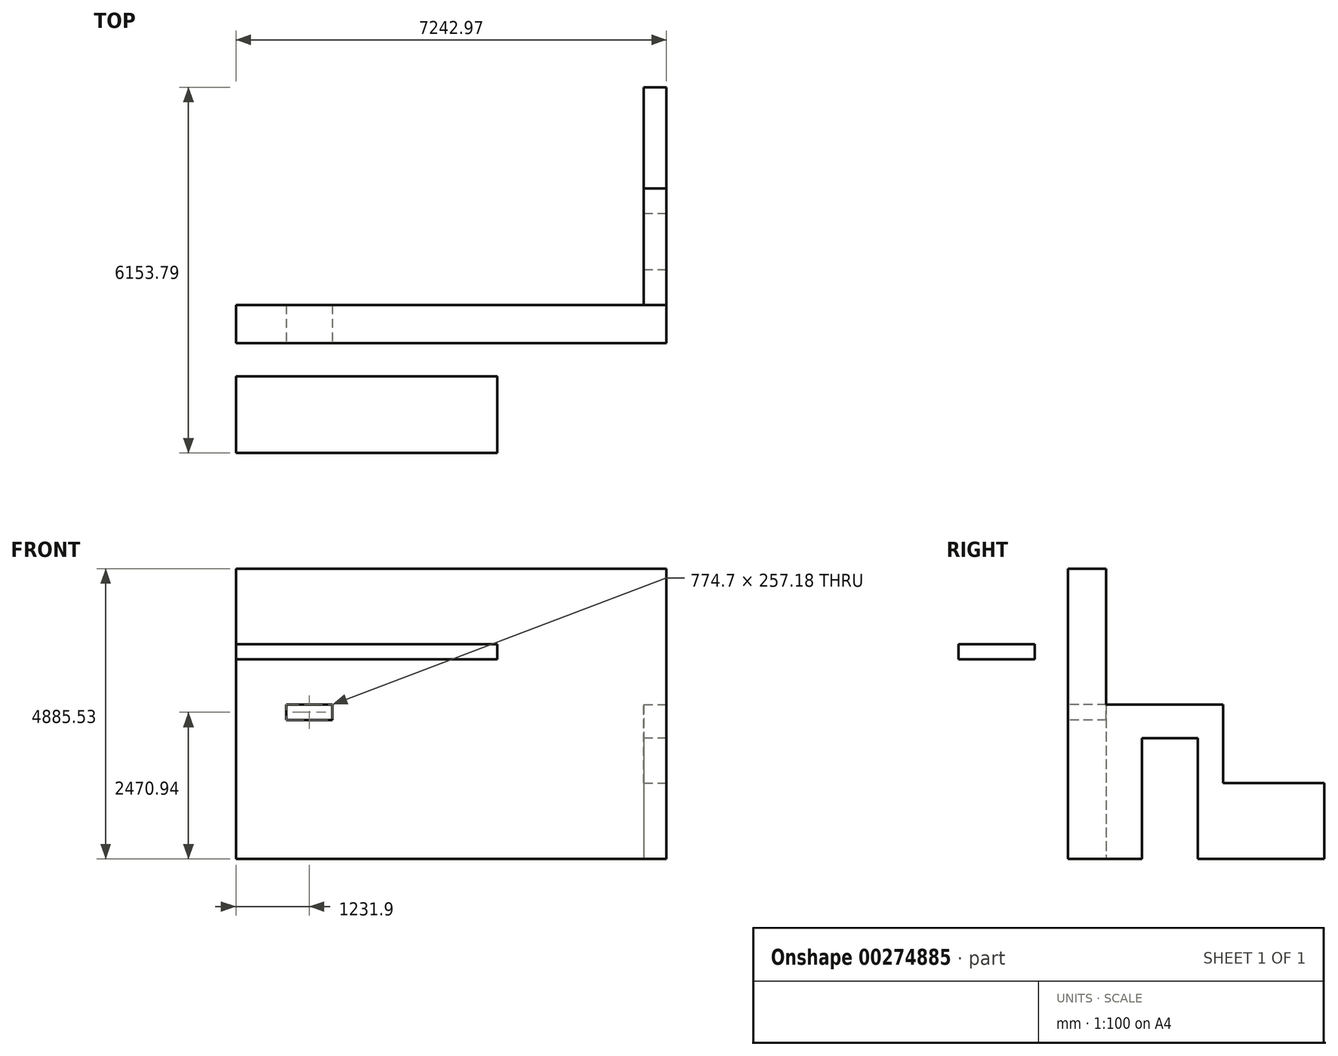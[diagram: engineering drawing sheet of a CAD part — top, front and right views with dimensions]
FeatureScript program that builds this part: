
annotation { "Feature Type Name" : "Feature", "Feature Type Description" : "" }
export const myFeature = defineFeature(function(context is Context, id is Id, definition is map)
    precondition{}
    {
        {
            var Q0;
            Q0=qCreatedBy(makeId("Top.planeOp"),FACE);
            var sketch = newSketch(context, id + "F0", { "sketchPlane" : qUnion([Q0])});
            skLineSegment(sketch, "E0.bottom", {"start": v(0, 0) * mm, "end": v(7268.37, 0) * mm});
            skLineSegment(sketch, "E0.top", {"start": v(0, 4074.32) * mm, "end": v(7268.37, 4074.32) * mm});
            skLineSegment(sketch, "E0.left", {"start": v(0, 0) * mm, "end": v(0, 4074.32) * mm});
            skLineSegment(sketch, "E0.right", {"start": v(7268.37, 0) * mm, "end": v(7268.37, 4074.32) * mm});
            skLineSegment(sketch, "E1.bottom", {"start": v(0, 0) * mm, "end": v(203.2, 0) * mm, "construction": true});
            skLineSegment(sketch, "E1.top", {"start": v(0, 203.2) * mm, "end": v(203.2, 203.2) * mm, "construction": true});
            skLineSegment(sketch, "E1.left", {"start": v(0, 0) * mm, "end": v(0, 203.2) * mm, "construction": true});
            skLineSegment(sketch, "E1.right", {"start": v(203.2, 0) * mm, "end": v(203.2, 203.2) * mm, "construction": true});
            skLineSegment(sketch, "E2.bottom", {"start": v(7268.37, 0) * mm, "end": v(7065.17, 0) * mm, "construction": true});
            skLineSegment(sketch, "E2.top", {"start": v(7268.37, 203.2) * mm, "end": v(7065.17, 203.2) * mm, "construction": true});
            skLineSegment(sketch, "E2.left", {"start": v(7268.37, 0) * mm, "end": v(7268.37, 203.2) * mm, "construction": true});
            skLineSegment(sketch, "E2.right", {"start": v(7065.17, 0) * mm, "end": v(7065.17, 203.2) * mm, "construction": true});
            skLineSegment(sketch, "E3.bottom", {"start": v(7268.37, 4074.32) * mm, "end": v(7065.17, 4074.32) * mm, "construction": true});
            skLineSegment(sketch, "E3.top", {"start": v(7268.37, 3871.12) * mm, "end": v(7065.17, 3871.12) * mm, "construction": true});
            skLineSegment(sketch, "E3.left", {"start": v(7268.37, 4074.32) * mm, "end": v(7268.37, 3871.12) * mm, "construction": true});
            skLineSegment(sketch, "E3.right", {"start": v(7065.17, 4074.32) * mm, "end": v(7065.17, 3871.12) * mm, "construction": true});
            skLineSegment(sketch, "E4.bottom", {"start": v(0, 4074.32) * mm, "end": v(203.2, 4074.32) * mm, "construction": true});
            skLineSegment(sketch, "E4.top", {"start": v(0, 3871.12) * mm, "end": v(203.2, 3871.12) * mm, "construction": true});
            skLineSegment(sketch, "E4.left", {"start": v(0, 4074.32) * mm, "end": v(0, 3871.12) * mm, "construction": true});
            skLineSegment(sketch, "E4.right", {"start": v(203.2, 4074.32) * mm, "end": v(203.2, 3871.12) * mm, "construction": true});
            skLineSegment(sketch, "E5.bottom", {"start": v(203.2, 3871.12) * mm, "end": v(7065.17, 3871.12) * mm});
            skLineSegment(sketch, "E5.top", {"start": v(203.2, 203.2) * mm, "end": v(7065.17, 203.2) * mm});
            skLineSegment(sketch, "E5.left", {"start": v(203.2, 3871.12) * mm, "end": v(203.2, 203.2) * mm});
            skLineSegment(sketch, "E5.right", {"start": v(7065.17, 3871.12) * mm, "end": v(7065.17, 203.2) * mm});
            skSolve(sketch);
        }
        {
            var Q0;
            Q0=makeQuery(id+"F0.imprint","IMPRINT",FACE,{"disambiguationData":[TD([[makeQuery(id+"F0.imprint","IMPRINT",EDGE,{"derivedFrom":sQuery(id+"F0.wireOp",EDGE,"E0.bottom")}),1.0]])]});
            extrude(context, id + "F1", {"entities" : qUnion([Q0]), "depth" : 2599.53 * mm});
        }
        {
            var Q0;
            Q0=qCreatedBy(makeId("Front.planeOp"),FACE);
            var sketch = newSketch(context, id + "F2", { "sketchPlane" : qUnion([Q0])});
            skLineSegment(sketch, "E6.bottom", {"start": v(0, 0) * mm, "end": v(1263.65, 0) * mm, "construction": true});
            skLineSegment(sketch, "E6.top", {"start": v(0, 2342.36) * mm, "end": v(1263.65, 2342.36) * mm, "construction": true});
            skLineSegment(sketch, "E6.left", {"start": v(0, 0) * mm, "end": v(0, 2342.36) * mm, "construction": true});
            skLineSegment(sketch, "E6.right", {"start": v(1263.65, 0) * mm, "end": v(1263.65, 2342.36) * mm, "construction": true});
            skLineSegment(sketch, "E7.bottom", {"start": v(1263.65, 2342.36) * mm, "end": v(1695.45, 2342.36) * mm});
            skLineSegment(sketch, "E7.top", {"start": v(1263.65, 2475.7) * mm, "end": v(1695.45, 2475.7) * mm});
            skLineSegment(sketch, "E7.left", {"start": v(1263.65, 2342.36) * mm, "end": v(1263.65, 2475.7) * mm});
            skLineSegment(sketch, "E7.right", {"start": v(1695.45, 2342.36) * mm, "end": v(1695.45, 2475.7) * mm});
            skSolve(sketch);
        }
        {
            var Q0;
            Q0=makeQuery(id+"F2.imprint","IMPRINT",FACE,{"disambiguationData":[TD([[makeQuery(id+"F2.imprint","IMPRINT",EDGE,{"derivedFrom":sQuery(id+"F2.wireOp",EDGE,"E7.bottom")}),1.0]])]});
            extrude(context, id + "F3", {"entities" : qUnion([Q0]), "operationType" : NewBodyOperationType.REMOVE, "oppositeDirection" : true, "depth" : 203.2 * mm});
        }
        {
            var Q0;
            Q0=makeQuery(id+"F1.opExtrude","SWEPT_FACE",FACE,{"disambiguationData":[OSD([sQuery(id+"F0.wireOp",EDGE,"E5.top")])]});
            var sketch = newSketch(context, id + "F4", { "sketchPlane" : qUnion([Q0])});
            skLineSegment(sketch, "E8.bottom", {"start": v(-7065.17, 0) * mm, "end": v(-6230.15, 0) * mm, "construction": true});
            skLineSegment(sketch, "E8.top", {"start": v(-7065.17, 2235.2) * mm, "end": v(-6230.15, 2235.2) * mm, "construction": true});
            skLineSegment(sketch, "E8.left", {"start": v(-7065.17, 0) * mm, "end": v(-7065.17, 2235.2) * mm, "construction": true});
            skLineSegment(sketch, "E8.right", {"start": v(-6230.15, 0) * mm, "end": v(-6230.15, 2235.2) * mm, "construction": true});
            skLineSegment(sketch, "E9.bottom", {"start": v(-6230.15, 2235.2) * mm, "end": v(-5925.35, 2235.2) * mm});
            skLineSegment(sketch, "E9.top", {"start": v(-6230.15, 2489.2) * mm, "end": v(-5925.35, 2489.2) * mm});
            skLineSegment(sketch, "E9.left", {"start": v(-6230.15, 2235.2) * mm, "end": v(-6230.15, 2489.2) * mm});
            skLineSegment(sketch, "E9.right", {"start": v(-5925.35, 2235.2) * mm, "end": v(-5925.35, 2489.2) * mm});
            skSolve(sketch);
        }
        {
            var Q0;
            Q0=makeQuery(id+"F4.imprint","IMPRINT",FACE,{"disambiguationData":[TD([[makeQuery(id+"F4.imprint","IMPRINT",EDGE,{"derivedFrom":sQuery(id+"F4.wireOp",EDGE,"E9.bottom")}),1.0]])]});
            extrude(context, id + "F5", {"entities" : qUnion([Q0]), "operationType" : NewBodyOperationType.REMOVE, "oppositeDirection" : true, "depth" : 203.2 * mm});
        }
        {
            var Q0;
            Q0=makeQuery(id+"F3.boolean.opBoolean","COPY",FACE,{"derivedFrom":makeQuery(id+"F3.opExtrude","SWEPT_FACE",FACE,{"disambiguationData":[OSD([sQuery(id+"F2.wireOp",EDGE,"E7.left")])]})});
            extrude(context, id + "F6", {"entities" : qUnion([Q0]), "operationType" : NewBodyOperationType.REMOVE, "oppositeDirection" : true, "depth" : 381 * mm});
        }
        {
            var Q0;
            Q0=makeQuery(id+"F5.boolean.opBoolean","COPY",FACE,{"derivedFrom":makeQuery(id+"F5.opExtrude","SWEPT_FACE",FACE,{"disambiguationData":[OSD([sQuery(id+"F4.wireOp",EDGE,"E9.bottom")])]})});
            var Q1;
            Q1=makeQuery(id+"F5.boolean.opBoolean","COPY",FACE,{"derivedFrom":makeQuery(id+"F5.opExtrude","SWEPT_FACE",FACE,{"disambiguationData":[OSD([sQuery(id+"F4.wireOp",EDGE,"E9.top")])]})});
            extrude(context, id + "F7", {"entities" : qUnion([Q0]), "operationType" : NewBodyOperationType.ADD, "endBound" : BoundingType.UP_TO_SURFACE, "endBoundEntityFace" : qUnion([Q1]), "depth" : 25.4 * mm});
        }
        {
            var Q0;
            {var subQ0=sQuery(id+"F2.wireOp",EDGE,"E7.top");Q0=makeQuery(id+"F6.boolean.opBoolean","MERGE",FACE,{"derivedFrom":[makeQuery(id+"F3.boolean.opBoolean","COPY",FACE,{"derivedFrom":makeQuery(id+"F3.opExtrude","SWEPT_FACE",FACE,{"disambiguationData":[OSD([subQ0])]})}),makeQuery(id+"F6.opExtrude","SWEPT_FACE",FACE,{"disambiguationData":[OSD([subQ0,sQuery(id+"F2.wireOp",EDGE,"E7.left")])]})]});}
            extrude(context, id + "F8", {"entities" : qUnion([Q0]), "operationType" : NewBodyOperationType.REMOVE, "oppositeDirection" : true, "depth" : 106.68 * mm});
        }
        {
            var Q0;
            {var subQ0=sQuery(id+"F2.wireOp",EDGE,"E7.left");var subQ1=sQuery(id+"F2.wireOp",EDGE,"E7.top");Q0=makeQuery(id+"F8.boolean.opBoolean","MERGE",FACE,{"derivedFrom":[makeQuery(id+"F6.boolean.opBoolean","COPY",FACE,{"derivedFrom":makeQuery(id+"F6.opExtrude","CAP_FACE",FACE,{"disambiguationData":[OSD([subQ0])],"isStart":false})}),makeQuery(id+"F8.opExtrude","SWEPT_FACE",FACE,{"disambiguationData":[OSD([subQ1,subQ0]),TDD([makeQuery(id+"F6.boolean.opBoolean","COPY",EDGE,{"derivedFrom":makeQuery(id+"F6.opExtrude","CAP_EDGE",EDGE,{"disambiguationData":[OSD([subQ1,subQ0])],"isStart":false})})])]})]});}
            extrude(context, id + "F9", {"entities" : qUnion([Q0]), "operationType" : NewBodyOperationType.REMOVE, "oppositeDirection" : true, "depth" : 38.1 * mm});
        }
        {
            var Q0;
            {var subQ0=sQuery(id+"F2.wireOp",EDGE,"E7.left");var subQ1=sQuery(id+"F2.wireOp",EDGE,"E7.top");Q0=makeQuery(id+"F9.boolean.opBoolean","MERGE",FACE,{"derivedFrom":[makeQuery(id+"F8.boolean.opBoolean","COPY",FACE,{"derivedFrom":makeQuery(id+"F8.opExtrude","CAP_FACE",FACE,{"disambiguationData":[OSD([subQ1,subQ0])],"isStart":false})}),makeQuery(id+"F9.opExtrude","SWEPT_FACE",FACE,{"disambiguationData":[OSD([subQ1,subQ0]),TDD([makeQuery(id+"F8.boolean.opBoolean","COPY",EDGE,{"derivedFrom":makeQuery(id+"F8.opExtrude","CAP_EDGE",EDGE,{"disambiguationData":[OSD([subQ1,subQ0]),TDD([makeQuery(id+"F6.boolean.opBoolean","COPY",EDGE,{"derivedFrom":makeQuery(id+"F6.opExtrude","CAP_EDGE",EDGE,{"disambiguationData":[OSD([subQ1,subQ0])],"isStart":false})})])],"isStart":false})})])]})]});}
            var Q1;
            Q1=makeQuery(id+"F1.opExtrude","CAP_FACE",FACE,{"disambiguationData":[OSD([sQuery(id+"F0.wireOp",EDGE,"E0.bottom"),sQuery(id+"F0.wireOp",EDGE,"E0.top"),sQuery(id+"F0.wireOp",EDGE,"E0.left"),sQuery(id+"F0.wireOp",EDGE,"E0.right"),sQuery(id+"F0.wireOp",EDGE,"E5.bottom"),sQuery(id+"F0.wireOp",EDGE,"E5.top"),sQuery(id+"F0.wireOp",EDGE,"E5.left"),sQuery(id+"F0.wireOp",EDGE,"E5.right")])],"isStart":false});
            extrude(context, id + "F10", {"entities" : qUnion([Q0]), "operationType" : NewBodyOperationType.REMOVE, "endBound" : BoundingType.UP_TO_SURFACE, "oppositeDirection" : true, "endBoundEntityFace" : qUnion([Q1]), "depth" : 25.4 * mm});
        }
        {
            var Q0;
            Q0=makeQuery(id+"F1.opExtrude","SWEPT_FACE",FACE,{"disambiguationData":[OSD([sQuery(id+"F0.wireOp",EDGE,"E5.right")])]});
            var sketch = newSketch(context, id + "F11", { "sketchPlane" : qUnion([Q0])});
            skLineSegment(sketch, "E10.bottom", {"start": v(-203.2, 0) * mm, "end": v(-803.28, 0) * mm, "construction": true});
            skLineSegment(sketch, "E10.top", {"start": v(-203.2, 531.94) * mm, "end": v(-803.28, 531.94) * mm, "construction": true});
            skLineSegment(sketch, "E10.left", {"start": v(-203.2, 0) * mm, "end": v(-203.2, 531.94) * mm, "construction": true});
            skLineSegment(sketch, "E10.right", {"start": v(-803.28, 0) * mm, "end": v(-803.28, 531.94) * mm, "construction": true});
            skLineSegment(sketch, "E11.bottom", {"start": v(-803.28, 0) * mm, "end": v(-1717.67, 0) * mm});
            skLineSegment(sketch, "E11.top", {"start": v(-803.28, 2082.8) * mm, "end": v(-1717.68, 2082.8) * mm});
            skLineSegment(sketch, "E11.left", {"start": v(-803.28, 0) * mm, "end": v(-803.28, 2082.8) * mm});
            skLineSegment(sketch, "E11.right", {"start": v(-1717.67, 0) * mm, "end": v(-1717.68, 2082.8) * mm});
            skSolve(sketch);
        }
        {
            var Q0;
            Q0=makeQuery(id+"F11.imprint","IMPRINT",FACE,{"disambiguationData":[TD([[makeQuery(id+"F11.imprint","IMPRINT",EDGE,{"derivedFrom":sQuery(id+"F11.wireOp",EDGE,"E11.bottom")}),1.0]])]});
            var Q1;
            Q1=makeQuery(id+"F1.opExtrude","SWEPT_FACE",FACE,{"disambiguationData":[OSD([sQuery(id+"F0.wireOp",EDGE,"E0.right")])]});
            extrude(context, id + "F12", {"entities" : qUnion([Q0]), "operationType" : NewBodyOperationType.REMOVE, "endBound" : BoundingType.UP_TO_SURFACE, "oppositeDirection" : true, "endBoundEntityFace" : qUnion([Q1]), "depth" : 25.4 * mm});
        }
        {
            var Q0;
            {var subQ0=sQuery(id+"F4.wireOp",EDGE,"E9.bottom");Q0=makeQuery(id+"F7.boolean.opBoolean","MERGE",FACE,{"derivedFrom":[makeQuery(id+"F1.opExtrude","SWEPT_FACE",FACE,{"disambiguationData":[OSD([sQuery(id+"F0.wireOp",EDGE,"E0.bottom")])]}),makeQuery(id+"F7.opExtrude","SWEPT_FACE",FACE,{"disambiguationData":[OSD([subQ0]),TDD([makeQuery(id+"F5.boolean.opBoolean","COPY",EDGE,{"derivedFrom":makeQuery(id+"F5.opExtrude","CAP_EDGE",EDGE,{"disambiguationData":[OSD([subQ0])],"isStart":false})})])]})]});}
            extrude(context, id + "F13", {"entities" : qUnion([Q0]), "operationType" : NewBodyOperationType.ADD, "depth" : 177.8 * mm});
        }
        {
            var Q0;
            {var subQ0=sQuery(id+"F2.wireOp",EDGE,"E7.left");var subQ1=sQuery(id+"F2.wireOp",EDGE,"E7.top");Q0=makeQuery(id+"F13.boolean.opBoolean","MERGE",FACE,{"derivedFrom":[makeQuery(id+"F10.boolean.opBoolean","MERGE",FACE,{"derivedFrom":[makeQuery(id+"F9.boolean.opBoolean","COPY",FACE,{"derivedFrom":makeQuery(id+"F9.opExtrude","CAP_FACE",FACE,{"disambiguationData":[OSD([subQ1,subQ0])],"isStart":false})})],"fromTools":[makeQuery(id+"F10.opExtrude","SWEPT_FACE",FACE,{"disambiguationData":[OSD([subQ1,subQ0]),TDD([makeQuery(id+"F9.boolean.opBoolean","COPY",EDGE,{"derivedFrom":makeQuery(id+"F9.opExtrude","CAP_EDGE",EDGE,{"disambiguationData":[OSD([subQ1,subQ0]),TDD([makeQuery(id+"F8.boolean.opBoolean","COPY",EDGE,{"derivedFrom":makeQuery(id+"F8.opExtrude","CAP_EDGE",EDGE,{"disambiguationData":[OSD([subQ1,subQ0]),TDD([makeQuery(id+"F6.boolean.opBoolean","COPY",EDGE,{"derivedFrom":makeQuery(id+"F6.opExtrude","CAP_EDGE",EDGE,{"disambiguationData":[OSD([subQ1,subQ0])],"isStart":false})})])],"isStart":false})})])],"isStart":false})})])]})]}),makeQuery(id+"F13.opExtrude","SWEPT_FACE",FACE,{"disambiguationData":[OSD([subQ1,subQ0])]})]});}
            extrude(context, id + "F14", {"entities" : qUnion([Q0]), "operationType" : NewBodyOperationType.ADD, "depth" : 203.2 * mm});
        }
        {
            var Q0;
            {var subQ0=sQuery(id+"F2.wireOp",EDGE,"E7.right");var subQ1=sQuery(id+"F2.wireOp",EDGE,"E7.top");Q0=makeQuery(id+"F13.boolean.opBoolean","MERGE",FACE,{"derivedFrom":[makeQuery(id+"F10.boolean.opBoolean","MERGE",FACE,{"derivedFrom":[makeQuery(id+"F8.boolean.opBoolean","MERGE",FACE,{"derivedFrom":[makeQuery(id+"F3.boolean.opBoolean","COPY",FACE,{"derivedFrom":makeQuery(id+"F3.opExtrude","SWEPT_FACE",FACE,{"disambiguationData":[OSD([subQ0])]})})],"fromTools":[makeQuery(id+"F8.opExtrude","SWEPT_FACE",FACE,{"disambiguationData":[OSD([subQ1,subQ0])]})]})],"fromTools":[makeQuery(id+"F10.opExtrude","SWEPT_FACE",FACE,{"disambiguationData":[OSD([subQ1,subQ0])]})]}),makeQuery(id+"F13.opExtrude","SWEPT_FACE",FACE,{"disambiguationData":[OSD([subQ1,subQ0])]})]});}
            extrude(context, id + "F15", {"entities" : qUnion([Q0]), "operationType" : NewBodyOperationType.REMOVE, "oppositeDirection" : true, "depth" : 127 * mm});
        }
        {
            var Q0;
            {var subQ0=sQuery(id+"F0.wireOp",EDGE,"E0.right");Q0=makeQuery(id+"F13.boolean.opBoolean","MERGE",FACE,{"derivedFrom":[makeQuery(id+"F1.opExtrude","SWEPT_FACE",FACE,{"disambiguationData":[OSD([subQ0])]}),makeQuery(id+"F13.opExtrude","SWEPT_FACE",FACE,{"disambiguationData":[OSD([sQuery(id+"F0.wireOp",EDGE,"E0.bottom"),subQ0])]})]});}
            var Q1;
            Q1=makeQuery(id+"F1.opExtrude","SWEPT_FACE",FACE,{"disambiguationData":[OSD([sQuery(id+"F0.wireOp",EDGE,"E5.right")])]});
            extrude(context, id + "F16", {"entities" : qUnion([Q0]), "operationType" : NewBodyOperationType.REMOVE, "endBound" : BoundingType.UP_TO_SURFACE, "oppositeDirection" : true, "endBoundEntityFace" : qUnion([Q1]), "depth" : 25.4 * mm});
        }
        {
            var Q0;
            {var subQ0=sQuery(id+"F0.wireOp",EDGE,"E0.left");Q0=makeQuery(id+"F13.boolean.opBoolean","MERGE",FACE,{"derivedFrom":[makeQuery(id+"F1.opExtrude","SWEPT_FACE",FACE,{"disambiguationData":[OSD([subQ0])]}),makeQuery(id+"F13.opExtrude","SWEPT_FACE",FACE,{"disambiguationData":[OSD([sQuery(id+"F0.wireOp",EDGE,"E0.bottom"),subQ0])]})]});}
            var Q1;
            Q1=makeQuery(id+"F1.opExtrude","SWEPT_FACE",FACE,{"disambiguationData":[OSD([sQuery(id+"F0.wireOp",EDGE,"E5.left")])]});
            extrude(context, id + "F17", {"entities" : qUnion([Q0]), "operationType" : NewBodyOperationType.REMOVE, "endBound" : BoundingType.UP_TO_SURFACE, "oppositeDirection" : true, "endBoundEntityFace" : qUnion([Q1]), "depth" : 25.4 * mm});
        }
        {
            var Q0;
            {var subQ0=sQuery(id+"F0.wireOp",EDGE,"E0.top");var subQ5=sQuery(id+"F0.wireOp",EDGE,"E0.right");var subQ7=sQuery(id+"F0.wireOp",EDGE,"E0.bottom");Q0=makeQuery(id+"F16.boolean.opBoolean","COPY",FACE,{"disambiguationData":[TD([makeQuery(id+"F1.opExtrude","SWEPT_FACE",FACE,{"disambiguationData":[OSD([subQ0])]})])],"derivedFrom":makeQuery(id+"F16.opExtrude","CAP_FACE",FACE,{"disambiguationData":[OSD([subQ7,subQ5])],"isStart":false})});}
            extrude(context, id + "F18", {"entities" : qUnion([Q0]), "operationType" : NewBodyOperationType.REMOVE, "endBound" : BoundingType.THROUGH_ALL, "oppositeDirection" : true, "depth" : 25.4 * mm});
        }
        {
            var Q0;
            {var subQ3=sQuery(id+"F0.wireOp",EDGE,"E5.top");var subQ5=sQuery(id+"F0.wireOp",EDGE,"E0.right");var subQ8=sQuery(id+"F0.wireOp",EDGE,"E0.bottom");Q0=makeQuery(id+"F16.boolean.opBoolean","COPY",FACE,{"disambiguationData":[TD([makeQuery(id+"F1.opExtrude","SWEPT_FACE",FACE,{"disambiguationData":[OSD([subQ3])]})])],"derivedFrom":makeQuery(id+"F16.opExtrude","CAP_FACE",FACE,{"disambiguationData":[OSD([subQ8,subQ5])],"isStart":false})});}
            extrude(context, id + "F19", {"entities" : qUnion([Q0]), "operationType" : NewBodyOperationType.ADD, "depth" : 381 * mm, "offsetDistance" : 25.4 * mm});
        }
        {
            var Q0;
            {var subQ0=sQuery(id+"F0.wireOp",EDGE,"E5.top");var subQ1=sQuery(id+"F2.wireOp",EDGE,"E7.left");var subQ2=sQuery(id+"F2.wireOp",EDGE,"E7.top");var subQ3=makeQuery(id+"F6.boolean.opBoolean","COPY",VERTEX,{"derivedFrom":makeQuery(id+"F6.opExtrude","CAP_VERTEX",VERTEX,{"disambiguationData":[OSD([subQ2,subQ1]),TDD([makeQuery(id+"F3.boolean.opBoolean","COPY",VERTEX,{"derivedFrom":makeQuery(id+"F3.opExtrude","CAP_VERTEX",VERTEX,{"disambiguationData":[OSD([subQ2,subQ1])],"isStart":false})})])],"isStart":false})});var subQ4=sQuery(id+"F4.wireOp",EDGE,"E9.bottom");Q0=makeQuery(id+"F19.boolean.opBoolean","MERGE",FACE,{"derivedFrom":[makeQuery(id+"F14.boolean.opBoolean","MERGE",FACE,{"derivedFrom":[makeQuery(id+"F7.boolean.opBoolean","MERGE",FACE,{"derivedFrom":[makeQuery(id+"F1.opExtrude","SWEPT_FACE",FACE,{"disambiguationData":[OSD([subQ0])]}),makeQuery(id+"F7.opExtrude","SWEPT_FACE",FACE,{"disambiguationData":[OSD([subQ4]),TDD([makeQuery(id+"F5.boolean.opBoolean","COPY",EDGE,{"derivedFrom":makeQuery(id+"F5.opExtrude","CAP_EDGE",EDGE,{"disambiguationData":[OSD([subQ4])],"isStart":true})})])]})]}),makeQuery(id+"F14.opExtrude","SWEPT_FACE",FACE,{"disambiguationData":[OSD([subQ2,subQ1]),TDD([makeQuery(id+"F10.boolean.opBoolean","MERGE",EDGE,{"derivedFrom":[makeQuery(id+"F9.boolean.opBoolean","COPY",EDGE,{"derivedFrom":makeQuery(id+"F9.opExtrude","CAP_EDGE",EDGE,{"disambiguationData":[OSD([subQ2,subQ1]),TDD([makeQuery(id+"F8.boolean.opBoolean","MERGE",EDGE,{"derivedFrom":[makeQuery(id+"F6.boolean.opBoolean","COPY",EDGE,{"derivedFrom":makeQuery(id+"F6.opExtrude","CAP_EDGE",EDGE,{"disambiguationData":[OSD([subQ1]),TDD([makeQuery(id+"F3.boolean.opBoolean","COPY",EDGE,{"derivedFrom":makeQuery(id+"F3.opExtrude","CAP_EDGE",EDGE,{"disambiguationData":[OSD([subQ1])],"isStart":false})})])],"isStart":false})})],"fromTools":[makeQuery(id+"F8.opExtrude","SWEPT_EDGE",EDGE,{"disambiguationData":[OSD([subQ2,subQ1]),TDD([subQ3])]})]})])],"isStart":false})})],"fromTools":[makeQuery(id+"F10.opExtrude","SWEPT_EDGE",EDGE,{"disambiguationData":[OSD([subQ2,subQ1]),TDD([makeQuery(id+"F9.boolean.opBoolean","COPY",VERTEX,{"derivedFrom":makeQuery(id+"F9.opExtrude","CAP_VERTEX",VERTEX,{"disambiguationData":[OSD([subQ2,subQ1]),TDD([makeQuery(id+"F8.boolean.opBoolean","COPY",VERTEX,{"derivedFrom":makeQuery(id+"F8.opExtrude","CAP_VERTEX",VERTEX,{"disambiguationData":[OSD([subQ2,subQ1]),TDD([subQ3])],"isStart":false})})])],"isStart":false})})])]})]})])]})]}),makeQuery(id+"F19.opExtrude","SWEPT_FACE",FACE,{"disambiguationData":[OSD([subQ0,sQuery(id+"F0.wireOp",EDGE,"E5.right")])]})]});}
            var sketch = newSketch(context, id + "F20", { "sketchPlane" : qUnion([Q0])});
            skLineSegment(sketch, "E12.bottom", {"start": v(-7446.17, 2599.53) * mm, "end": v(-7065.17, 2599.53) * mm});
            skLineSegment(sketch, "E12.top", {"start": v(-7446.17, 0) * mm, "end": v(-7065.17, 0) * mm});
            skLineSegment(sketch, "E12.left", {"start": v(-7446.17, 2599.53) * mm, "end": v(-7446.17, 0) * mm});
            skLineSegment(sketch, "E12.right", {"start": v(-7065.17, 2599.53) * mm, "end": v(-7065.17, 0) * mm});
            skSolve(sketch);
        }
        {
            var Q0;
            Q0=makeQuery(id+"F20.imprint","IMPRINT",FACE,{"disambiguationData":[TD([[makeQuery(id+"F20.imprint","IMPRINT",EDGE,{"derivedFrom":sQuery(id+"F20.wireOp",EDGE,"E12.bottom")}),1.0]])]});
            extrude(context, id + "F21", {"entities" : qUnion([Q0]), "operationType" : NewBodyOperationType.ADD, "depth" : 600.07 * mm, "offsetDistance" : 25.4 * mm});
        }
        {
            var Q0;
            Q0=makeQuery(id+"F21.opExtrude","CAP_FACE",FACE,{"disambiguationData":[OSD([sQuery(id+"F20.wireOp",EDGE,"E12.bottom"),sQuery(id+"F20.wireOp",EDGE,"E12.top"),sQuery(id+"F20.wireOp",EDGE,"E12.left"),sQuery(id+"F20.wireOp",EDGE,"E12.right")])],"isStart":false});
            var sketch = newSketch(context, id + "F22", { "sketchPlane" : qUnion([Q0])});
            skLineSegment(sketch, "E13", {"start": v(-7446.17, 0) * mm, "end": v(-7446.17, 2032) * mm, "construction": true});
            skLineSegment(sketch, "E14.bottom", {"start": v(-7446.17, 2032) * mm, "end": v(-7065.17, 2032) * mm});
            skLineSegment(sketch, "E14.top", {"start": v(-7446.17, 2599.53) * mm, "end": v(-7065.17, 2599.53) * mm});
            skLineSegment(sketch, "E14.left", {"start": v(-7446.17, 2032) * mm, "end": v(-7446.17, 2599.53) * mm});
            skLineSegment(sketch, "E14.right", {"start": v(-7065.17, 2032) * mm, "end": v(-7065.17, 2599.53) * mm});
            skSolve(sketch);
        }
        {
            var Q0;
            Q0=makeQuery(id+"F22.imprint","IMPRINT",FACE,{"disambiguationData":[TD([[makeQuery(id+"F22.imprint","IMPRINT",EDGE,{"derivedFrom":sQuery(id+"F22.wireOp",EDGE,"E14.bottom")}),1.0]])]});
            extrude(context, id + "F23", {"entities" : qUnion([Q0]), "operationType" : NewBodyOperationType.ADD, "depth" : 812.8 * mm, "offsetDistance" : 25.4 * mm});
        }
        {
            var Q0;
            Q0=makeQuery(id+"F23.opExtrude","CAP_FACE",FACE,{"disambiguationData":[OSD([sQuery(id+"F22.wireOp",EDGE,"E14.bottom"),sQuery(id+"F22.wireOp",EDGE,"E14.top"),sQuery(id+"F22.wireOp",EDGE,"E14.left"),sQuery(id+"F22.wireOp",EDGE,"E14.right")])],"isStart":false});
            var sketch = newSketch(context, id + "F24", { "sketchPlane" : qUnion([Q0])});
            skLineSegment(sketch, "E15.bottom", {"start": v(-7446.17, 2599.53) * mm, "end": v(-7065.17, 2599.53) * mm});
            skLineSegment(sketch, "E15.top", {"start": v(-7446.17, 0) * mm, "end": v(-7065.17, 0) * mm});
            skLineSegment(sketch, "E15.left", {"start": v(-7446.17, 2599.53) * mm, "end": v(-7446.17, 0) * mm});
            skLineSegment(sketch, "E15.right", {"start": v(-7065.17, 2599.53) * mm, "end": v(-7065.17, 0) * mm});
            skSolve(sketch);
        }
        {
            var Q0;
            {var subQ0=sQuery(id+"F24.wireOp",EDGE,"E15.top");Q0=makeQuery(id+"F24.imprint","IMPRINT",FACE,{"disambiguationData":[TD([[makeQuery(id+"F24.imprint","IMPRINT",EDGE,{"derivedFrom":subQ0}),1.0]])]});}
            var Q1;
            {var subQ0=sQuery(id+"F24.wireOp",EDGE,"E15.bottom");Q1=makeQuery(id+"F24.imprint","IMPRINT",FACE,{"disambiguationData":[TD([[makeQuery(id+"F24.imprint","IMPRINT",EDGE,{"derivedFrom":subQ0}),1.0]])]});}
            extrude(context, id + "F25", {"entities" : qUnion([Q0, Q1]), "operationType" : NewBodyOperationType.ADD, "depth" : 2254.89 * mm, "offsetDistance" : 25.4 * mm});
        }
        {
            var Q0;
            {var subQ2=sQuery(id+"F0.wireOp",EDGE,"E0.left");var subQ3=sQuery(id+"F0.wireOp",EDGE,"E5.top");var subQ4=sQuery(id+"F0.wireOp",EDGE,"E0.right");var subQ5=sQuery(id+"F0.wireOp",EDGE,"E0.bottom");var subQ6=makeQuery(id+"F1.opExtrude","CAP_FACE",FACE,{"disambiguationData":[OSD([subQ5,sQuery(id+"F0.wireOp",EDGE,"E0.top"),subQ2,subQ4,sQuery(id+"F0.wireOp",EDGE,"E5.bottom"),subQ3,sQuery(id+"F0.wireOp",EDGE,"E5.left"),sQuery(id+"F0.wireOp",EDGE,"E5.right")])],"isStart":false});var subQ8=sQuery(id+"F2.wireOp",EDGE,"E7.left");var subQ9=sQuery(id+"F2.wireOp",EDGE,"E7.top");var subQ10=makeQuery(id+"F9.boolean.opBoolean","COPY",EDGE,{"derivedFrom":makeQuery(id+"F9.opExtrude","CAP_EDGE",EDGE,{"disambiguationData":[OSD([subQ9,subQ8]),TDD([makeQuery(id+"F8.boolean.opBoolean","COPY",EDGE,{"derivedFrom":makeQuery(id+"F8.opExtrude","CAP_EDGE",EDGE,{"disambiguationData":[OSD([subQ9,subQ8]),TDD([makeQuery(id+"F6.boolean.opBoolean","COPY",EDGE,{"derivedFrom":makeQuery(id+"F6.opExtrude","CAP_EDGE",EDGE,{"disambiguationData":[OSD([subQ9,subQ8])],"isStart":false})})])],"isStart":false})})])],"isStart":false})});var subQ11=makeQuery(id+"F1.opExtrude","CAP_EDGE",EDGE,{"disambiguationData":[OSD([subQ5])],"isStart":false});var subQ12=makeQuery(id+"F13.opExtrude","SWEPT_FACE",FACE,{"disambiguationData":[OSD([subQ5]),TDD([makeQuery(id+"F10.boolean.opBoolean","SPLIT",EDGE,{"disambiguationData":[TD([makeQuery(id+"F1.opExtrude","SWEPT_FACE",FACE,{"disambiguationData":[OSD([subQ2])]})])],"derivedFrom":subQ11})])]});var subQ16=makeQuery(id+"F1.opExtrude","SWEPT_FACE",FACE,{"disambiguationData":[OSD([subQ3])]});var subQ17=sQuery(id+"F2.wireOp",EDGE,"E7.right");var subQ18=makeQuery(id+"F13.opExtrude","SWEPT_FACE",FACE,{"disambiguationData":[OSD([subQ5]),TDD([makeQuery(id+"F10.boolean.opBoolean","SPLIT",EDGE,{"disambiguationData":[TD([makeQuery(id+"F1.opExtrude","SWEPT_FACE",FACE,{"disambiguationData":[OSD([subQ4])]})])],"derivedFrom":subQ11})])]});var subQ21=makeQuery(id+"F14.opExtrude","SWEPT_FACE",FACE,{"disambiguationData":[OSD([subQ9,subQ8]),TDD([makeQuery(id+"F13.boolean.opBoolean","MERGE",EDGE,{"derivedFrom":[makeQuery(id+"F10.boolean.opBoolean","COPY",EDGE,{"derivedFrom":makeQuery(id+"F10.opExtrude","CAP_EDGE",EDGE,{"disambiguationData":[OSD([subQ9,subQ8]),TDD([subQ10])],"isStart":false})}),makeQuery(id+"F13.opExtrude","SWEPT_EDGE",EDGE,{"disambiguationData":[OSD([subQ9,subQ8])]})]})])]});Q0=makeQuery(id+"F25.boolean.opBoolean","MERGE",FACE,{"derivedFrom":[makeQuery(id+"F23.boolean.opBoolean","MERGE",FACE,{"derivedFrom":[makeQuery(id+"F21.boolean.opBoolean","MERGE",FACE,{"derivedFrom":[makeQuery(id+"F19.boolean.opBoolean","MERGE",FACE,{"derivedFrom":[makeQuery(id+"F16.boolean.opBoolean","SPLIT",FACE,{"disambiguationData":[TD([makeQuery(id+"F15.boolean.opBoolean","COPY",FACE,{"derivedFrom":makeQuery(id+"F15.opExtrude","CAP_FACE",FACE,{"disambiguationData":[OSD([subQ9,subQ17])],"isStart":false})})])],"derivedFrom":makeQuery(id+"F14.boolean.opBoolean","MERGE",FACE,{"derivedFrom":[makeQuery(id+"F13.boolean.opBoolean","MERGE",FACE,{"derivedFrom":[subQ6,subQ12,subQ18]}),subQ21]})}),makeQuery(id+"F19.opExtrude","SWEPT_FACE",FACE,{"disambiguationData":[OSD([subQ5,subQ4]),TDD([makeQuery(id+"F16.boolean.opBoolean","COPY",EDGE,{"disambiguationData":[TD([subQ16])],"derivedFrom":makeQuery(id+"F16.opExtrude","CAP_EDGE",EDGE,{"disambiguationData":[OSD([subQ5,subQ4]),TDD([makeQuery(id+"F13.boolean.opBoolean","MERGE",EDGE,{"derivedFrom":[makeQuery(id+"F1.opExtrude","CAP_EDGE",EDGE,{"disambiguationData":[OSD([subQ4])],"isStart":false}),makeQuery(id+"F13.opExtrude","SWEPT_EDGE",EDGE,{"disambiguationData":[OSD([subQ5,subQ4]),TDD([makeQuery(id+"F1.opExtrude","CAP_VERTEX",VERTEX,{"disambiguationData":[OSD([subQ5,subQ4])],"isStart":false})])]})]})])],"isStart":false})})])]})]}),makeQuery(id+"F21.opExtrude","SWEPT_FACE",FACE,{"disambiguationData":[OSD([sQuery(id+"F20.wireOp",EDGE,"E12.bottom")])]})]}),makeQuery(id+"F23.opExtrude","SWEPT_FACE",FACE,{"disambiguationData":[OSD([sQuery(id+"F22.wireOp",EDGE,"E14.top")])]})]}),makeQuery(id+"F25.opExtrude","SWEPT_FACE",FACE,{"disambiguationData":[OSD([sQuery(id+"F24.wireOp",EDGE,"E15.bottom")])]})]});}
            var sketch = newSketch(context, id + "F26", { "sketchPlane" : qUnion([Q0])});
            skLineSegment(sketch, "E16.bottom", {"start": v(7065.17, 3870.96) * mm, "end": v(7446.17, 3870.96) * mm});
            skLineSegment(sketch, "E16.top", {"start": v(7065.17, 2444.88) * mm, "end": v(7446.17, 2444.88) * mm});
            skLineSegment(sketch, "E16.left", {"start": v(7065.17, 3870.96) * mm, "end": v(7065.17, 2444.88) * mm});
            skLineSegment(sketch, "E16.right", {"start": v(7446.17, 3870.96) * mm, "end": v(7446.17, 2444.88) * mm});
            skSolve(sketch);
        }
        {
            var Q0;
            Q0=makeQuery(id+"F26.imprint","IMPRINT",FACE,{"disambiguationData":[TD([[makeQuery(id+"F26.imprint","IMPRINT",EDGE,{"derivedFrom":sQuery(id+"F26.wireOp",EDGE,"E16.bottom")}),-1.0]])]});
            extrude(context, id + "F27", {"entities" : qUnion([Q0]), "operationType" : NewBodyOperationType.REMOVE, "oppositeDirection" : true, "depth" : 1320.8 * mm, "offsetDistance" : 25.4 * mm});
        }
        {
            var Q0;
            Q0=makeQuery(id+"F27.boolean.opBoolean","COPY",FACE,{"derivedFrom":makeQuery(id+"F27.opExtrude","SWEPT_FACE",FACE,{"disambiguationData":[OSD([sQuery(id+"F26.wireOp",EDGE,"E16.top")])]})});
            extrude(context, id + "F28", {"entities" : qUnion([Q0]), "operationType" : NewBodyOperationType.REMOVE, "oppositeDirection" : true, "depth" : 403.86 * mm, "offsetDistance" : 25.4 * mm});
        }
        {
            var Q0;
            Q0=makeQuery(id+"F25.opExtrude","CAP_FACE",FACE,{"disambiguationData":[OSD([sQuery(id+"F24.wireOp",EDGE,"E15.bottom"),sQuery(id+"F24.wireOp",EDGE,"E15.top"),sQuery(id+"F24.wireOp",EDGE,"E15.left"),sQuery(id+"F24.wireOp",EDGE,"E15.right")])],"isStart":true});
            extrude(context, id + "F29", {"entities" : qUnion([Q0]), "operationType" : NewBodyOperationType.REMOVE, "oppositeDirection" : true, "depth" : 127 * mm, "offsetDistance" : 25.4 * mm});
        }
        {
            var Q0;
            Q0=makeQuery(id+"F28.boolean.opBoolean","COPY",FACE,{"derivedFrom":makeQuery(id+"F28.opExtrude","CAP_FACE",FACE,{"disambiguationData":[OSD([sQuery(id+"F26.wireOp",EDGE,"E16.top")])],"isStart":false})});
            extrude(context, id + "F30", {"entities" : qUnion([Q0]), "operationType" : NewBodyOperationType.ADD, "depth" : 127 * mm, "offsetDistance" : 25.4 * mm});
        }
        {
            var Q0;
            {var subQ0=sQuery(id+"F2.wireOp",EDGE,"E7.left");var subQ1=sQuery(id+"F2.wireOp",EDGE,"E7.top");var subQ6=sQuery(id+"F0.wireOp",EDGE,"E0.bottom");var subQ9=sQuery(id+"F0.wireOp",EDGE,"E5.top");var subQ10=makeQuery(id+"F1.opExtrude","SWEPT_FACE",FACE,{"disambiguationData":[OSD([subQ9])]});var subQ12=sQuery(id+"F0.wireOp",EDGE,"E0.left");var subQ13=sQuery(id+"F0.wireOp",EDGE,"E5.left");var subQ14=sQuery(id+"F0.wireOp",EDGE,"E0.top");var subQ15=makeQuery(id+"F1.opExtrude","SWEPT_FACE",FACE,{"disambiguationData":[OSD([subQ12])]});var subQ16=sQuery(id+"F0.wireOp",EDGE,"E5.bottom");var subQ17=sQuery(id+"F0.wireOp",EDGE,"E0.right");var subQ18=makeQuery(id+"F9.boolean.opBoolean","COPY",EDGE,{"derivedFrom":makeQuery(id+"F9.opExtrude","CAP_EDGE",EDGE,{"disambiguationData":[OSD([subQ1,subQ0]),TDD([makeQuery(id+"F8.boolean.opBoolean","COPY",EDGE,{"derivedFrom":makeQuery(id+"F8.opExtrude","CAP_EDGE",EDGE,{"disambiguationData":[OSD([subQ1,subQ0]),TDD([makeQuery(id+"F6.boolean.opBoolean","COPY",EDGE,{"derivedFrom":makeQuery(id+"F6.opExtrude","CAP_EDGE",EDGE,{"disambiguationData":[OSD([subQ1,subQ0])],"isStart":false})})])],"isStart":false})})])],"isStart":false})});var subQ20=makeQuery(id+"F1.opExtrude","CAP_FACE",FACE,{"disambiguationData":[OSD([subQ6,subQ14,subQ12,subQ17,subQ16,subQ9,subQ13,sQuery(id+"F0.wireOp",EDGE,"E5.right")])],"isStart":false});var subQ23=makeQuery(id+"F1.opExtrude","CAP_EDGE",EDGE,{"disambiguationData":[OSD([subQ6])],"isStart":false});Q0=makeQuery(id+"F17.boolean.opBoolean","SPLIT",FACE,{"disambiguationData":[TD([subQ10])],"derivedFrom":makeQuery(id+"F16.boolean.opBoolean","SPLIT",FACE,{"disambiguationData":[TD([makeQuery(id+"F1.opExtrude","SWEPT_FACE",FACE,{"disambiguationData":[OSD([subQ14])]})])],"derivedFrom":makeQuery(id+"F14.boolean.opBoolean","MERGE",FACE,{"derivedFrom":[makeQuery(id+"F13.boolean.opBoolean","MERGE",FACE,{"derivedFrom":[subQ20,makeQuery(id+"F13.opExtrude","SWEPT_FACE",FACE,{"disambiguationData":[OSD([subQ6]),TDD([makeQuery(id+"F10.boolean.opBoolean","SPLIT",EDGE,{"disambiguationData":[TD([subQ15])],"derivedFrom":subQ23})])]}),makeQuery(id+"F13.opExtrude","SWEPT_FACE",FACE,{"disambiguationData":[OSD([subQ6]),TDD([makeQuery(id+"F10.boolean.opBoolean","SPLIT",EDGE,{"disambiguationData":[TD([makeQuery(id+"F1.opExtrude","SWEPT_FACE",FACE,{"disambiguationData":[OSD([subQ17])]})])],"derivedFrom":subQ23})])]})]}),makeQuery(id+"F14.opExtrude","SWEPT_FACE",FACE,{"disambiguationData":[OSD([subQ1,subQ0]),TDD([makeQuery(id+"F13.boolean.opBoolean","MERGE",EDGE,{"derivedFrom":[makeQuery(id+"F10.boolean.opBoolean","COPY",EDGE,{"derivedFrom":makeQuery(id+"F10.opExtrude","CAP_EDGE",EDGE,{"disambiguationData":[OSD([subQ1,subQ0]),TDD([subQ18])],"isStart":false})}),makeQuery(id+"F13.opExtrude","SWEPT_EDGE",EDGE,{"disambiguationData":[OSD([subQ1,subQ0])]})]})])]})]})})});}
            extrude(context, id + "F31", {"entities" : qUnion([Q0]), "operationType" : NewBodyOperationType.ADD, "depth" : 2286 * mm, "offsetDistance" : 25.4 * mm});
        }
        {
            var Q0;
            {var subQ0=sQuery(id+"F2.wireOp",EDGE,"E7.left");var subQ1=sQuery(id+"F2.wireOp",EDGE,"E7.top");var subQ2=sQuery(id+"F0.wireOp",EDGE,"E0.bottom");var subQ3=sQuery(id+"F0.wireOp",EDGE,"E0.right");Q0=makeQuery(id+"F31.boolean.opBoolean","MERGE",FACE,{"derivedFrom":[makeQuery(id+"F19.boolean.opBoolean","MERGE",FACE,{"derivedFrom":[makeQuery(id+"F14.boolean.opBoolean","MERGE",FACE,{"derivedFrom":[makeQuery(id+"F13.opExtrude","CAP_FACE",FACE,{"disambiguationData":[OSD([subQ2,sQuery(id+"F4.wireOp",EDGE,"E9.bottom")])],"isStart":false}),makeQuery(id+"F14.opExtrude","SWEPT_FACE",FACE,{"disambiguationData":[OSD([subQ1,subQ0]),TDD([makeQuery(id+"F13.opExtrude","CAP_EDGE",EDGE,{"disambiguationData":[OSD([subQ1,subQ0])],"isStart":false})])]})]}),makeQuery(id+"F19.opExtrude","SWEPT_FACE",FACE,{"disambiguationData":[OSD([subQ2,subQ3]),TDD([makeQuery(id+"F16.boolean.opBoolean","COPY",EDGE,{"derivedFrom":makeQuery(id+"F16.opExtrude","CAP_EDGE",EDGE,{"disambiguationData":[OSD([subQ2,subQ3]),TDD([makeQuery(id+"F13.opExtrude","CAP_EDGE",EDGE,{"disambiguationData":[OSD([subQ2,subQ3])],"isStart":false})])],"isStart":false})})])]})]}),makeQuery(id+"F31.opExtrude","SWEPT_FACE",FACE,{"disambiguationData":[OSD([subQ2,subQ1,subQ0])]})]});}
            var sketch = newSketch(context, id + "F32", { "sketchPlane" : qUnion([Q0])});
            skLineSegment(sketch, "E17.bottom", {"start": v(1047.75, 2599.53) * mm, "end": v(7446.17, 2599.53) * mm});
            skLineSegment(sketch, "E17.top", {"start": v(1047.75, 4885.53) * mm, "end": v(7446.17, 4885.53) * mm});
            skLineSegment(sketch, "E17.left", {"start": v(1047.75, 2599.53) * mm, "end": v(1047.75, 4885.53) * mm});
            skLineSegment(sketch, "E17.right", {"start": v(7446.17, 2599.53) * mm, "end": v(7446.17, 4885.53) * mm});
            skSolve(sketch);
        }
        {
            var Q0;
            Q0=makeQuery(id+"F32.imprint","IMPRINT",FACE,{"disambiguationData":[TD([[makeQuery(id+"F32.imprint","IMPRINT",EDGE,{"derivedFrom":sQuery(id+"F32.wireOp",EDGE,"E17.top")}),-1.0]])]});
            var Q1;
            {var subQ0=sQuery(id+"F2.wireOp",EDGE,"E7.left");var subQ1=sQuery(id+"F2.wireOp",EDGE,"E7.top");var subQ2=sQuery(id+"F0.wireOp",EDGE,"E5.top");var subQ3=makeQuery(id+"F6.boolean.opBoolean","COPY",VERTEX,{"derivedFrom":makeQuery(id+"F6.opExtrude","CAP_VERTEX",VERTEX,{"disambiguationData":[OSD([subQ1,subQ0]),TDD([makeQuery(id+"F3.boolean.opBoolean","COPY",VERTEX,{"derivedFrom":makeQuery(id+"F3.opExtrude","CAP_VERTEX",VERTEX,{"disambiguationData":[OSD([subQ1,subQ0])],"isStart":false})})])],"isStart":false})});var subQ4=sQuery(id+"F4.wireOp",EDGE,"E9.bottom");Q1=makeQuery(id+"F31.boolean.opBoolean","MERGE",FACE,{"derivedFrom":[makeQuery(id+"F19.boolean.opBoolean","MERGE",FACE,{"derivedFrom":[makeQuery(id+"F14.boolean.opBoolean","MERGE",FACE,{"derivedFrom":[makeQuery(id+"F7.boolean.opBoolean","MERGE",FACE,{"derivedFrom":[makeQuery(id+"F1.opExtrude","SWEPT_FACE",FACE,{"disambiguationData":[OSD([subQ2])]}),makeQuery(id+"F7.opExtrude","SWEPT_FACE",FACE,{"disambiguationData":[OSD([subQ4]),TDD([makeQuery(id+"F5.boolean.opBoolean","COPY",EDGE,{"derivedFrom":makeQuery(id+"F5.opExtrude","CAP_EDGE",EDGE,{"disambiguationData":[OSD([subQ4])],"isStart":true})})])]})]}),makeQuery(id+"F14.opExtrude","SWEPT_FACE",FACE,{"disambiguationData":[OSD([subQ1,subQ0]),TDD([makeQuery(id+"F10.boolean.opBoolean","MERGE",EDGE,{"derivedFrom":[makeQuery(id+"F9.boolean.opBoolean","COPY",EDGE,{"derivedFrom":makeQuery(id+"F9.opExtrude","CAP_EDGE",EDGE,{"disambiguationData":[OSD([subQ1,subQ0]),TDD([makeQuery(id+"F8.boolean.opBoolean","MERGE",EDGE,{"derivedFrom":[makeQuery(id+"F6.boolean.opBoolean","COPY",EDGE,{"derivedFrom":makeQuery(id+"F6.opExtrude","CAP_EDGE",EDGE,{"disambiguationData":[OSD([subQ0]),TDD([makeQuery(id+"F3.boolean.opBoolean","COPY",EDGE,{"derivedFrom":makeQuery(id+"F3.opExtrude","CAP_EDGE",EDGE,{"disambiguationData":[OSD([subQ0])],"isStart":false})})])],"isStart":false})})],"fromTools":[makeQuery(id+"F8.opExtrude","SWEPT_EDGE",EDGE,{"disambiguationData":[OSD([subQ1,subQ0]),TDD([subQ3])]})]})])],"isStart":false})})],"fromTools":[makeQuery(id+"F10.opExtrude","SWEPT_EDGE",EDGE,{"disambiguationData":[OSD([subQ1,subQ0]),TDD([makeQuery(id+"F9.boolean.opBoolean","COPY",VERTEX,{"derivedFrom":makeQuery(id+"F9.opExtrude","CAP_VERTEX",VERTEX,{"disambiguationData":[OSD([subQ1,subQ0]),TDD([makeQuery(id+"F8.boolean.opBoolean","COPY",VERTEX,{"derivedFrom":makeQuery(id+"F8.opExtrude","CAP_VERTEX",VERTEX,{"disambiguationData":[OSD([subQ1,subQ0]),TDD([subQ3])],"isStart":false})})])],"isStart":false})})])]})]})])]})]}),makeQuery(id+"F19.opExtrude","SWEPT_FACE",FACE,{"disambiguationData":[OSD([subQ2,sQuery(id+"F0.wireOp",EDGE,"E5.right")])]})]}),makeQuery(id+"F31.opExtrude","SWEPT_FACE",FACE,{"disambiguationData":[OSD([subQ2,subQ1,subQ0])]})]});}
            extrude(context, id + "F33", {"entities" : qUnion([Q0]), "operationType" : NewBodyOperationType.ADD, "endBound" : BoundingType.UP_TO_SURFACE, "oppositeDirection" : true, "depth" : 25.4 * mm, "endBoundEntityFace" : qUnion([Q1]), "offsetDistance" : 25.4 * mm});
        }
        {
            var Q0;
            {var subQ0=sQuery(id+"F0.wireOp",EDGE,"E0.left");var subQ1=sQuery(id+"F0.wireOp",EDGE,"E0.bottom");var subQ5=sQuery(id+"F0.wireOp",EDGE,"E5.top");Q0=makeQuery(id+"F31.boolean.opBoolean","MERGE",FACE,{"derivedFrom":[makeQuery(id+"F17.boolean.opBoolean","COPY",FACE,{"disambiguationData":[TD([makeQuery(id+"F1.opExtrude","SWEPT_FACE",FACE,{"disambiguationData":[OSD([subQ5])]})])],"derivedFrom":makeQuery(id+"F17.opExtrude","CAP_FACE",FACE,{"disambiguationData":[OSD([subQ1,subQ0])],"isStart":false})}),makeQuery(id+"F31.opExtrude","SWEPT_FACE",FACE,{"disambiguationData":[OSD([subQ1,subQ0])]})]});}
            var sketch = newSketch(context, id + "F34", { "sketchPlane" : qUnion([Q0])});
            skLineSegment(sketch, "E18", {"start": v(177.8, 0) * mm, "end": v(736.6, 0) * mm, "construction": true});
            skLineSegment(sketch, "E19", {"start": v(736.6, 0) * mm, "end": v(736.6, 3614.5) * mm, "construction": true});
            skLineSegment(sketch, "E20.bottom", {"start": v(736.6, 3614.5) * mm, "end": v(2022.48, 3614.5) * mm});
            skLineSegment(sketch, "E20.top", {"start": v(736.6, 3359.13) * mm, "end": v(2022.48, 3359.13) * mm});
            skLineSegment(sketch, "E20.left", {"start": v(736.6, 3614.5) * mm, "end": v(736.6, 3359.13) * mm});
            skLineSegment(sketch, "E20.right", {"start": v(2022.48, 3614.5) * mm, "end": v(2022.48, 3359.13) * mm});
            skSolve(sketch);
        }
        {
            var Q0;
            Q0=makeQuery(id+"F34.imprint","IMPRINT",FACE,{"disambiguationData":[TD([[makeQuery(id+"F34.imprint","IMPRINT",EDGE,{"derivedFrom":sQuery(id+"F34.wireOp",EDGE,"E20.bottom")}),-1.0]])]});
            extrude(context, id + "F35", {"entities" : qUnion([Q0]), "oppositeDirection" : true, "depth" : 4394.2 * mm, "offsetDistance" : 25.4 * mm});
        }
        {
            var Q0;
            {var subQ0=sQuery(id+"F2.wireOp",EDGE,"E7.left");var subQ1=sQuery(id+"F2.wireOp",EDGE,"E7.top");var subQ2=sQuery(id+"F0.wireOp",EDGE,"E5.top");var subQ3=makeQuery(id+"F6.boolean.opBoolean","COPY",VERTEX,{"derivedFrom":makeQuery(id+"F6.opExtrude","CAP_VERTEX",VERTEX,{"disambiguationData":[OSD([subQ1,subQ0]),TDD([makeQuery(id+"F3.boolean.opBoolean","COPY",VERTEX,{"derivedFrom":makeQuery(id+"F3.opExtrude","CAP_VERTEX",VERTEX,{"disambiguationData":[OSD([subQ1,subQ0])],"isStart":false})})])],"isStart":false})});var subQ4=sQuery(id+"F4.wireOp",EDGE,"E9.bottom");Q0=makeQuery(id+"F33.boolean.opBoolean","MERGE",FACE,{"derivedFrom":[makeQuery(id+"F31.boolean.opBoolean","MERGE",FACE,{"derivedFrom":[makeQuery(id+"F19.boolean.opBoolean","MERGE",FACE,{"derivedFrom":[makeQuery(id+"F14.boolean.opBoolean","MERGE",FACE,{"derivedFrom":[makeQuery(id+"F7.boolean.opBoolean","MERGE",FACE,{"derivedFrom":[makeQuery(id+"F1.opExtrude","SWEPT_FACE",FACE,{"disambiguationData":[OSD([subQ2])]}),makeQuery(id+"F7.opExtrude","SWEPT_FACE",FACE,{"disambiguationData":[OSD([subQ4]),TDD([makeQuery(id+"F5.boolean.opBoolean","COPY",EDGE,{"derivedFrom":makeQuery(id+"F5.opExtrude","CAP_EDGE",EDGE,{"disambiguationData":[OSD([subQ4])],"isStart":true})})])]})]}),makeQuery(id+"F14.opExtrude","SWEPT_FACE",FACE,{"disambiguationData":[OSD([subQ1,subQ0]),TDD([makeQuery(id+"F10.boolean.opBoolean","MERGE",EDGE,{"derivedFrom":[makeQuery(id+"F9.boolean.opBoolean","COPY",EDGE,{"derivedFrom":makeQuery(id+"F9.opExtrude","CAP_EDGE",EDGE,{"disambiguationData":[OSD([subQ1,subQ0]),TDD([makeQuery(id+"F8.boolean.opBoolean","MERGE",EDGE,{"derivedFrom":[makeQuery(id+"F6.boolean.opBoolean","COPY",EDGE,{"derivedFrom":makeQuery(id+"F6.opExtrude","CAP_EDGE",EDGE,{"disambiguationData":[OSD([subQ0]),TDD([makeQuery(id+"F3.boolean.opBoolean","COPY",EDGE,{"derivedFrom":makeQuery(id+"F3.opExtrude","CAP_EDGE",EDGE,{"disambiguationData":[OSD([subQ0])],"isStart":false})})])],"isStart":false})})],"fromTools":[makeQuery(id+"F8.opExtrude","SWEPT_EDGE",EDGE,{"disambiguationData":[OSD([subQ1,subQ0]),TDD([subQ3])]})]})])],"isStart":false})})],"fromTools":[makeQuery(id+"F10.opExtrude","SWEPT_EDGE",EDGE,{"disambiguationData":[OSD([subQ1,subQ0]),TDD([makeQuery(id+"F9.boolean.opBoolean","COPY",VERTEX,{"derivedFrom":makeQuery(id+"F9.opExtrude","CAP_VERTEX",VERTEX,{"disambiguationData":[OSD([subQ1,subQ0]),TDD([makeQuery(id+"F8.boolean.opBoolean","COPY",VERTEX,{"derivedFrom":makeQuery(id+"F8.opExtrude","CAP_VERTEX",VERTEX,{"disambiguationData":[OSD([subQ1,subQ0]),TDD([subQ3])],"isStart":false})})])],"isStart":false})})])]})]})])]})]}),makeQuery(id+"F19.opExtrude","SWEPT_FACE",FACE,{"disambiguationData":[OSD([subQ2,sQuery(id+"F0.wireOp",EDGE,"E5.right")])]})]}),makeQuery(id+"F31.opExtrude","SWEPT_FACE",FACE,{"disambiguationData":[OSD([subQ2,subQ1,subQ0])]})]}),makeQuery(id+"F33.opExtrude","CAP_FACE",FACE,{"disambiguationData":[OSD([sQuery(id+"F32.wireOp",EDGE,"E17.bottom"),sQuery(id+"F32.wireOp",EDGE,"E17.top"),sQuery(id+"F32.wireOp",EDGE,"E17.left"),sQuery(id+"F32.wireOp",EDGE,"E17.right")])],"isStart":false})]});}
            extrude(context, id + "F36", {"entities" : qUnion([Q0]), "operationType" : NewBodyOperationType.ADD, "depth" : 260.35 * mm, "offsetDistance" : 25.4 * mm});
        }
        {
            var Q0;
            Q0=makeQuery(id+"F30.opExtrude","CAP_FACE",FACE,{"disambiguationData":[OSD([sQuery(id+"F26.wireOp",EDGE,"E16.top")])],"isStart":false});
            var Q1;
            Q1=makeQuery(id+"F21.opExtrude","CAP_FACE",FACE,{"disambiguationData":[OSD([sQuery(id+"F20.wireOp",EDGE,"E12.bottom"),sQuery(id+"F20.wireOp",EDGE,"E12.top"),sQuery(id+"F20.wireOp",EDGE,"E12.left"),sQuery(id+"F20.wireOp",EDGE,"E12.right")])],"isStart":false});
            extrude(context, id + "F37", {"entities" : qUnion([Q0, Q1]), "operationType" : NewBodyOperationType.ADD, "depth" : 260.35 * mm, "offsetDistance" : 25.4 * mm});
        }
        {
            var Q0;
            Q0=makeQuery(id+"F29.boolean.opBoolean","COPY",FACE,{"derivedFrom":makeQuery(id+"F29.opExtrude","CAP_FACE",FACE,{"disambiguationData":[OSD([sQuery(id+"F24.wireOp",EDGE,"E15.bottom"),sQuery(id+"F24.wireOp",EDGE,"E15.top"),sQuery(id+"F24.wireOp",EDGE,"E15.left"),sQuery(id+"F24.wireOp",EDGE,"E15.right")])],"isStart":false})});
            extrude(context, id + "F38", {"entities" : qUnion([Q0]), "operationType" : NewBodyOperationType.REMOVE, "oppositeDirection" : true, "depth" : 260.35 * mm, "offsetDistance" : 25.4 * mm});
        }
        {
            var Q0;
            Q0=makeQuery(id+"F25.opExtrude","CAP_FACE",FACE,{"disambiguationData":[OSD([sQuery(id+"F24.wireOp",EDGE,"E15.bottom"),sQuery(id+"F24.wireOp",EDGE,"E15.top"),sQuery(id+"F24.wireOp",EDGE,"E15.left"),sQuery(id+"F24.wireOp",EDGE,"E15.right")])],"isStart":false});
            extrude(context, id + "F39", {"entities" : qUnion([Q0]), "operationType" : NewBodyOperationType.ADD, "depth" : 260.35 * mm, "offsetDistance" : 25.4 * mm});
        }
    });
